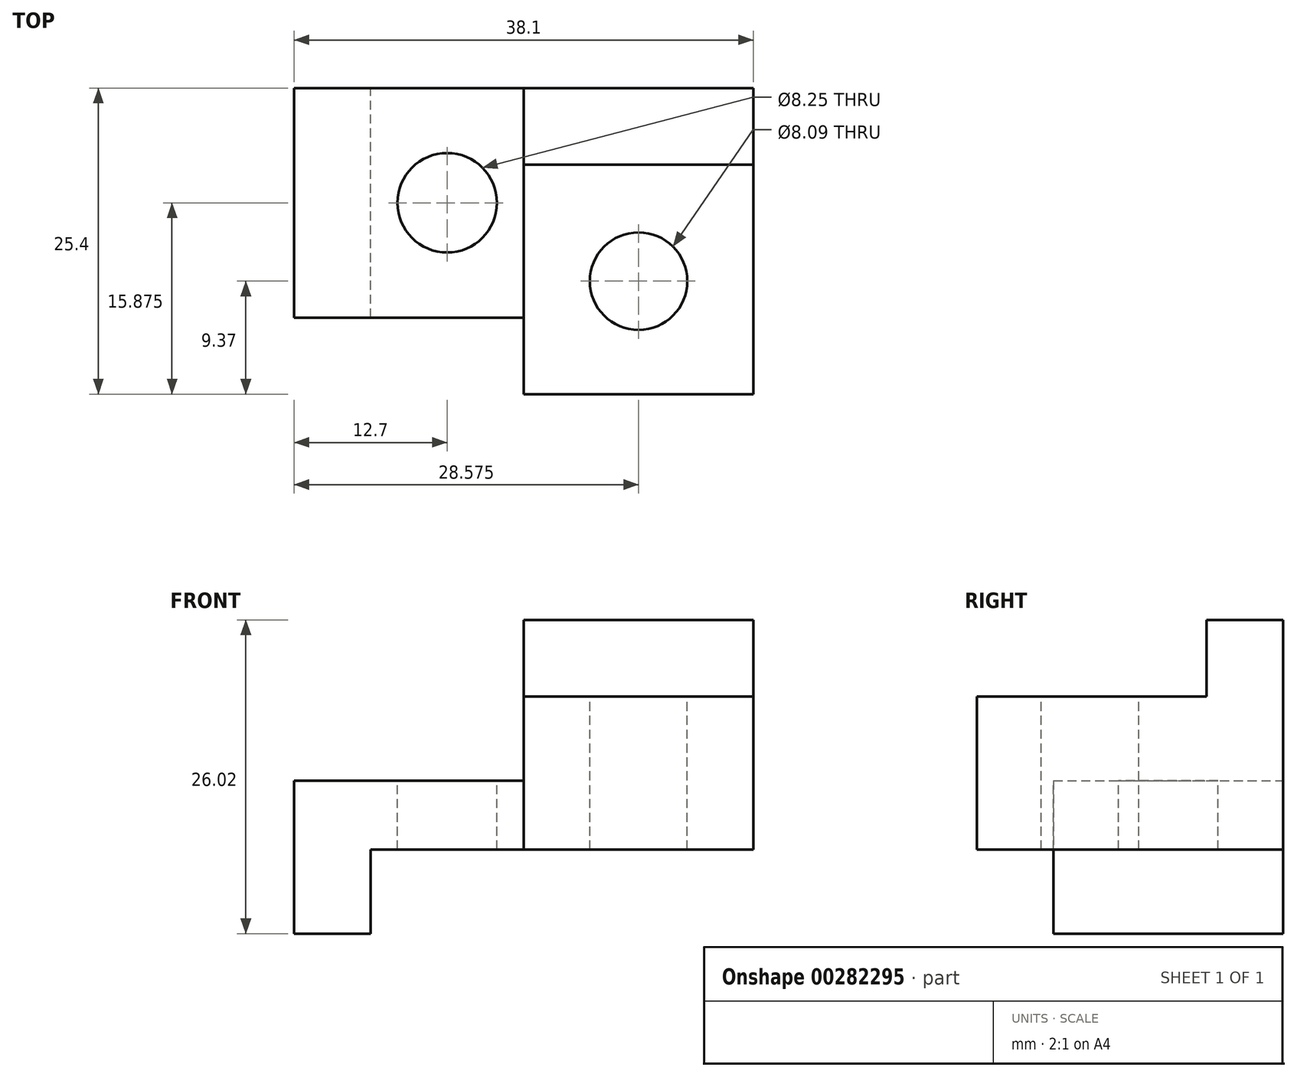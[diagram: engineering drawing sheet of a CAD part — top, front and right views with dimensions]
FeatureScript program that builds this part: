
annotation { "Feature Type Name" : "Feature", "Feature Type Description" : "" }
export const myFeature = defineFeature(function(context is Context, id is Id, definition is map)
    precondition{}
    {
        {
            var Q0;
            Q0=qCreatedBy(makeId("Right.planeOp"),FACE);
            var sketch = newSketch(context, id + "F0", { "sketchPlane" : qUnion([Q0])});
            skLineSegment(sketch, "E0", {"start": v(0, 6.97) * mm, "end": v(0, -5.73) * mm});
            skLineSegment(sketch, "E1", {"start": v(0, -5.73) * mm, "end": v(25.4, -5.73) * mm});
            skLineSegment(sketch, "E2", {"start": v(25.4, -5.73) * mm, "end": v(25.4, 13.32) * mm});
            skLineSegment(sketch, "E3", {"start": v(25.4, 13.32) * mm, "end": v(19.05, 13.32) * mm});
            skLineSegment(sketch, "E4", {"start": v(19.05, 13.32) * mm, "end": v(19.05, 6.97) * mm});
            skLineSegment(sketch, "E5", {"start": v(19.05, 6.97) * mm, "end": v(0, 6.97) * mm});
            skSolve(sketch);
        }
        {
            var Q0;
            Q0 = qSketchRegion(id + "F0", true);
            extrude(context, id + "F1", {"entities" : qUnion([Q0]), "depth" : 19.05 * mm});
        }
        {
            var Q0;
            Q0=makeQuery(id+"F1.opExtrude","SWEPT_FACE",FACE,{"disambiguationData":[OSD([sQuery(id+"F0.wireOp",EDGE,"E2")])]});
            var sketch = newSketch(context, id + "F2", { "sketchPlane" : qUnion([Q0])});
            skLineSegment(sketch, "E6", {"start": v(0, -5.73) * mm, "end": v(0, 0) * mm});
            skLineSegment(sketch, "E7", {"start": v(0, 0) * mm, "end": v(19.05, 0) * mm});
            skLineSegment(sketch, "E8", {"start": v(19.05, 0) * mm, "end": v(19.05, -12.7) * mm});
            skLineSegment(sketch, "E9", {"start": v(19.05, -12.7) * mm, "end": v(12.7, -12.7) * mm});
            skLineSegment(sketch, "E10", {"start": v(12.7, -12.7) * mm, "end": v(12.7, -5.73) * mm});
            skLineSegment(sketch, "E11", {"start": v(12.7, -5.73) * mm, "end": v(0, -5.73) * mm});
            skSolve(sketch);
        }
        {
            var Q0;
            Q0 = qSketchRegion(id + "F2", true);
            extrude(context, id + "F3", {"entities" : qUnion([Q0]), "oppositeDirection" : true, "depth" : 19.05 * mm});
        }
        {
            var Q0;
            Q0=makeQuery(id+"F1.opExtrude","SWEPT_FACE",FACE,{"disambiguationData":[OSD([sQuery(id+"F0.wireOp",EDGE,"E5")])]});
            var sketch = newSketch(context, id + "F4", { "sketchPlane" : qUnion([Q0])});
            skCircle(sketch, "E12", {"center": v(9.53, 9.37) * mm, "radius": 4.04 * mm});
            skSolve(sketch);
        }
        {
            var Q0;
            Q0 = qSketchRegion(id + "F4", true);
            extrude(context, id + "F5", {"entities" : qUnion([Q0]), "operationType" : NewBodyOperationType.REMOVE, "oppositeDirection" : true, "depth" : 25.4 * mm});
        }
        {
            var Q0;
            Q0=makeQuery(id+"F3.opExtrude","SWEPT_FACE",FACE,{"disambiguationData":[OSD([sQuery(id+"F2.wireOp",EDGE,"E7")])]});
            var sketch = newSketch(context, id + "F6", { "sketchPlane" : qUnion([Q0])});
            skCircle(sketch, "E13", {"center": v(-6.35, 15.88) * mm, "radius": 4.12 * mm});
            skSolve(sketch);
        }
        {
            var Q0;
            Q0 = qSketchRegion(id + "F6", true);
            extrude(context, id + "F7", {"entities" : qUnion([Q0]), "operationType" : NewBodyOperationType.REMOVE, "oppositeDirection" : true, "depth" : 25.4 * mm});
        }
    });
